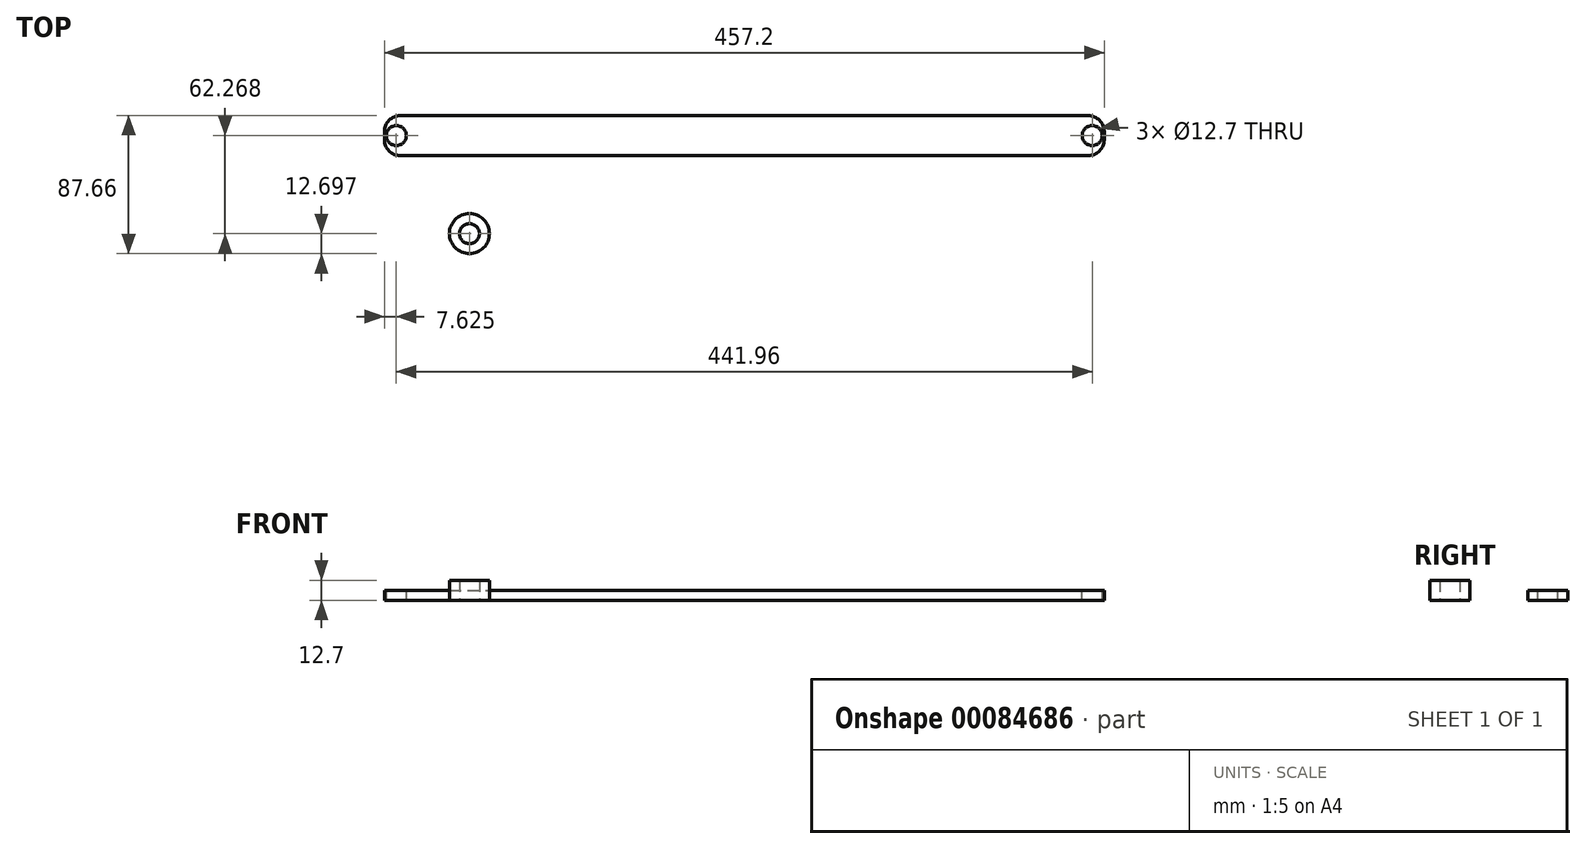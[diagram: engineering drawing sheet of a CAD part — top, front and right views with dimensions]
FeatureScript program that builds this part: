
annotation { "Feature Type Name" : "Feature", "Feature Type Description" : "" }
export const myFeature = defineFeature(function(context is Context, id is Id, definition is map)
    precondition{}
    {
        {
            var Q0;
            Q0=qCreatedBy(makeId("Top.planeOp"),FACE);
            var sketch = newSketch(context, id + "F0", { "sketchPlane" : qUnion([Q0])});
            skLineSegment(sketch, "E0.bottom", {"start": v(-36.75, 38.64) * mm, "end": v(420.45, 38.64) * mm});
            skLineSegment(sketch, "E0.top", {"start": v(-36.75, 13.24) * mm, "end": v(420.45, 13.24) * mm});
            skLineSegment(sketch, "E0.left", {"start": v(-36.75, 38.64) * mm, "end": v(-36.75, 13.24) * mm});
            skLineSegment(sketch, "E0.right", {"start": v(420.45, 38.64) * mm, "end": v(420.45, 13.24) * mm});
            skSolve(sketch);
        }
        {
            var Q0;
            Q0=makeQuery(id+"F0.imprint","IMPRINT",FACE,{"disambiguationData":[TD([[makeQuery(id+"F0.imprint","IMPRINT",EDGE,{"derivedFrom":sQuery(id+"F0.wireOp",EDGE,"E0.bottom")}),-1.0]])]});
            extrude(context, id + "F1", {"entities" : qUnion([Q0]), "depth" : 6.35 * mm});
        }
        {
            var Q0;
            Q0=makeQuery(id+"F1.opExtrude","CAP_FACE",FACE,{"disambiguationData":[OSD([sQuery(id+"F0.wireOp",EDGE,"E0.bottom"),sQuery(id+"F0.wireOp",EDGE,"E0.top"),sQuery(id+"F0.wireOp",EDGE,"E0.left"),sQuery(id+"F0.wireOp",EDGE,"E0.right")])],"isStart":false});
            var sketch = newSketch(context, id + "F2", { "sketchPlane" : qUnion([Q0])});
            skCircle(sketch, "E1", {"center": v(-29.13, 25.94) * mm, "radius": 6.35 * mm});
            skPoint(sketch, "E1.centerSnap0", {"position": v(-36.75, 25.94) * mm});
            skCircle(sketch, "E2", {"center": v(412.83, 25.94) * mm, "radius": 6.35 * mm});
            skPoint(sketch, "E2.centerSnap0", {"position": v(420.45, 25.94) * mm});
            skSolve(sketch);
        }
        {
            var Q0;
            Q0 = qSketchRegion(id + "F2", true);
            extrude(context, id + "F3", {"entities" : qUnion([Q0]), "operationType" : NewBodyOperationType.REMOVE, "oppositeDirection" : true, "depth" : 25.4 * mm});
        }
        {
            var Q0;
            Q0=qCreatedBy(makeId("Top.planeOp"),FACE);
            var sketch = newSketch(context, id + "F4", { "sketchPlane" : qUnion([Q0])});
            skCircle(sketch, "E3", {"center": v(17.28, -36.32) * mm, "radius": 12.7 * mm});
            skCircle(sketch, "E4", {"center": v(17.28, -36.32) * mm, "radius": 6.35 * mm});
            skSolve(sketch);
        }
        {
            var Q0;
            Q0=makeQuery(id+"F4.imprint","IMPRINT",FACE,{"disambiguationData":[TD([[makeQuery(id+"F4.imprint","IMPRINT",EDGE,{"derivedFrom":sQuery(id+"F4.wireOp",EDGE,"E3")}),1.0]])]});
            extrude(context, id + "F5", {"entities" : qUnion([Q0]), "depth" : 12.7 * mm});
        }
        {
            var Q0;
            Q0=makeQuery(id+"F1.opExtrude","SWEPT_EDGE",EDGE,{"disambiguationData":[OSD([sQuery(id+"F0.wireOp",EDGE,"E0.top"),sQuery(id+"F0.wireOp",EDGE,"E0.left")])]});
            var Q1;
            Q1=makeQuery(id+"F1.opExtrude","SWEPT_EDGE",EDGE,{"disambiguationData":[OSD([sQuery(id+"F0.wireOp",EDGE,"E0.bottom"),sQuery(id+"F0.wireOp",EDGE,"E0.left")])]});
            var Q2;
            Q2=makeQuery(id+"F1.opExtrude","SWEPT_EDGE",EDGE,{"disambiguationData":[OSD([sQuery(id+"F0.wireOp",EDGE,"E0.bottom"),sQuery(id+"F0.wireOp",EDGE,"E0.right")])]});
            var Q3;
            Q3=makeQuery(id+"F1.opExtrude","SWEPT_EDGE",EDGE,{"disambiguationData":[OSD([sQuery(id+"F0.wireOp",EDGE,"E0.top"),sQuery(id+"F0.wireOp",EDGE,"E0.right")])]});
            fillet(context, id + "F6", {"entities" : qUnion([Q0, Q1, Q2, Q3]), "radius" : 10.16 * mm, "tangentPropagation" : true, "allowEdgeOverflow" : false});
        }
    });
